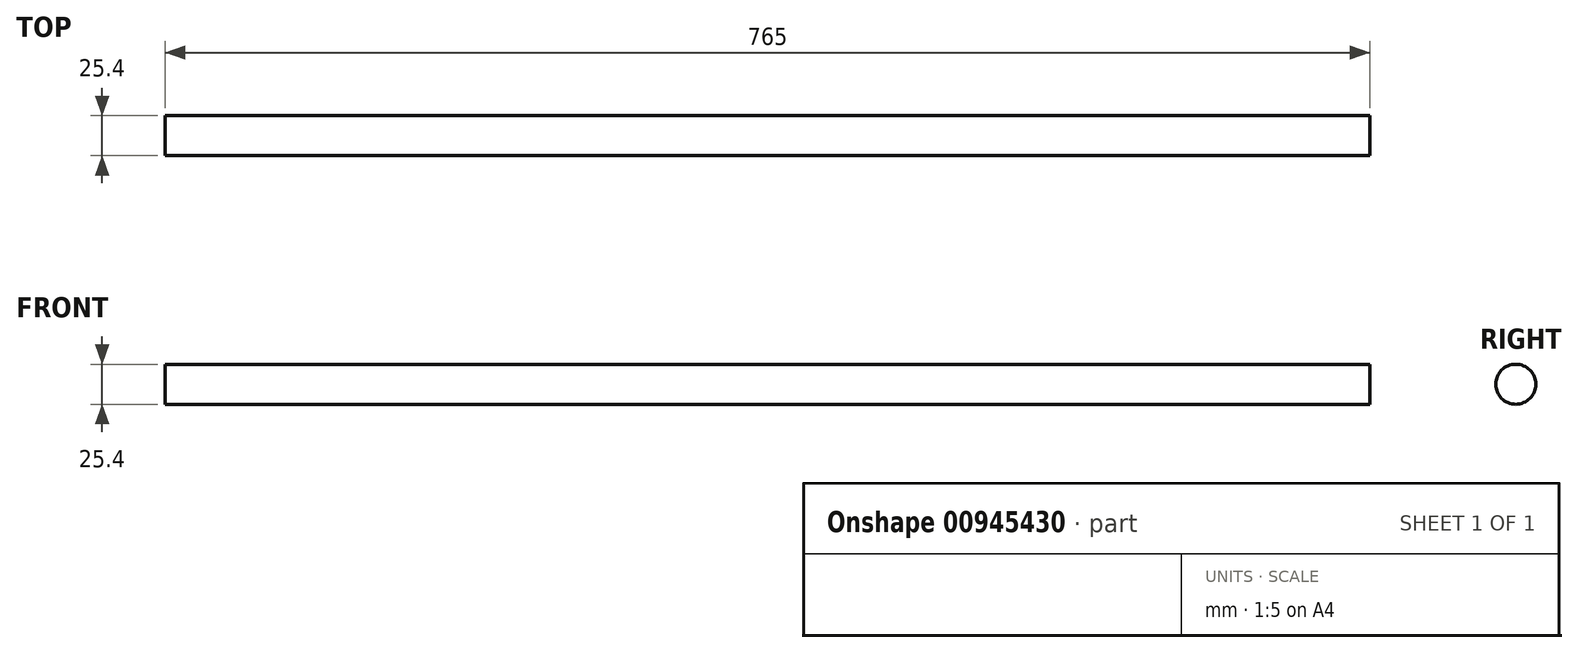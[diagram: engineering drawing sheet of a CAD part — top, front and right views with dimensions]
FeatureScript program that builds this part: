
annotation { "Feature Type Name" : "Feature", "Feature Type Description" : "" }
export const myFeature = defineFeature(function(context is Context, id is Id, definition is map)
    precondition{}
    {
        {
            var Q0;
            Q0=qCreatedBy(makeId("Right.planeOp"),FACE);
            var sketch = newSketch(context, id + "F0", { "sketchPlane" : qUnion([Q0])});
            skCircle(sketch, "E0", {"center": v(0, 0) * mm, "radius": 12.7 * mm});
            skSolve(sketch);
        }
        {
            var Q0;
            Q0=sQuery(id+"F0.wireOp",EDGE,"E0");
            extrude(context, id + "F1", {"bodyType" : ToolBodyType.SURFACE, "surfaceEntities" : qUnion([Q0]), "depth" : 765 * mm, "offsetDistance" : 25.4 * mm});
        }
    });
